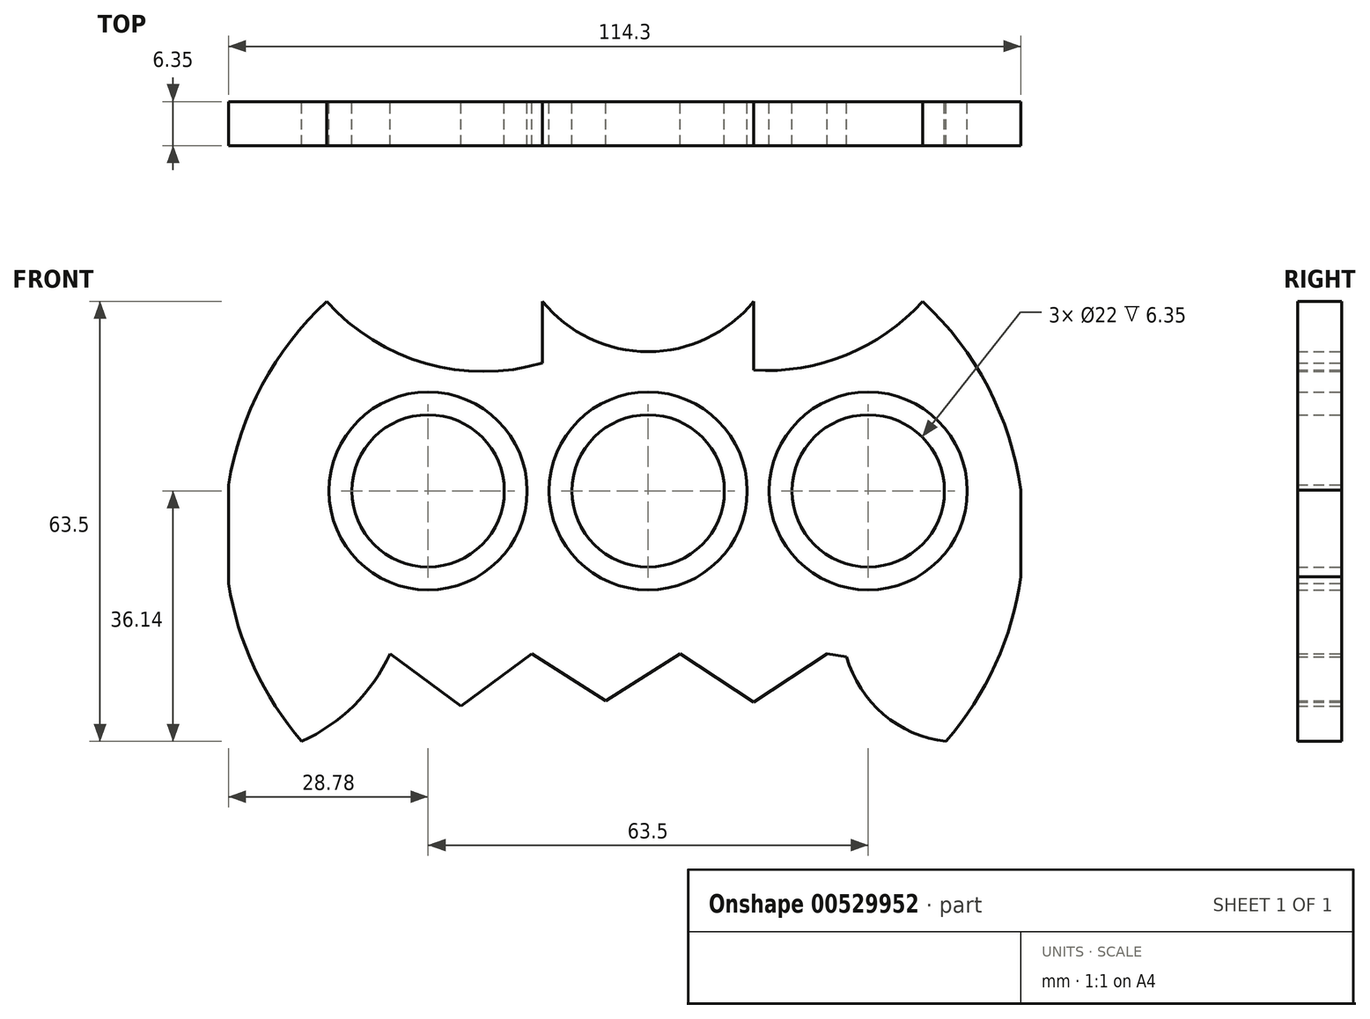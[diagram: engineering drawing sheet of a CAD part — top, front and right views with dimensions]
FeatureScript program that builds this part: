
annotation { "Feature Type Name" : "Feature", "Feature Type Description" : "" }
export const myFeature = defineFeature(function(context is Context, id is Id, definition is map)
    precondition{}
    {
        {
            var Q0;
            Q0=qCreatedBy(makeId("Front.planeOp"),FACE);
            var sketch = newSketch(context, id + "F0", { "sketchPlane" : qUnion([Q0])});
            skCircle(sketch, "E0", {"center": v(0, 0) * mm, "radius": 14.29 * mm});
            skCircle(sketch, "E1", {"center": v(0, 0) * mm, "radius": 11 * mm});
            skCircle(sketch, "E2", {"center": v(-31.75, 0) * mm, "radius": 14.29 * mm});
            skCircle(sketch, "E3", {"center": v(-31.75, 0) * mm, "radius": 11 * mm});
            skCircle(sketch, "E4", {"center": v(31.75, 0) * mm, "radius": 14.29 * mm});
            skCircle(sketch, "E5", {"center": v(31.75, 0) * mm, "radius": 11 * mm});
            skSolve(sketch);
        }
        {
            var Q0;
            Q0=qCreatedBy(makeId("Front.planeOp"),FACE);
            var sketch = newSketch(context, id + "F1", { "sketchPlane" : qUnion([Q0])});
            skArc(sketch, "E6.0", {"start": v(-46.36, 27.36) * mm, "mid": v(-61.02, -3.66) * mm, "end": v(-49.97, -36.14) * mm});
            skArc(sketch, "E7.0", {"start": v(-46.36, 27.36) * mm, "mid": v(-32.1, 18.4) * mm, "end": v(-15.24, 18.47) * mm});
            skPoint(sketch, "E8.0", {"position": v(-15.24, 22.92) * mm});
            skArc(sketch, "E9.0", {"start": v(-15.24, 27.36) * mm, "mid": v(0, 20.1) * mm, "end": v(15.24, 27.36) * mm});
            skPoint(sketch, "E10.0", {"position": v(28.55, 19.61) * mm});
            skArc(sketch, "E11.0", {"start": v(42.97, -36.14) * mm, "mid": v(54.13, -3.7) * mm, "end": v(39.6, 27.36) * mm});
            skLineSegment(sketch, "E12.0.0", {"start": v(25.82, -23.5) * mm, "end": v(28.64, -23.93) * mm});
            skArc(sketch, "E12.0.1", {"start": v(28.64, -23.93) * mm, "mid": v(33.92, -32.24) * mm, "end": v(42.97, -36.14) * mm});
            skArc(sketch, "E12.0.2", {"start": v(42.97, -36.14) * mm, "mid": v(50.1, -25.04) * mm, "end": v(53.77, -12.37) * mm});
            skLineSegment(sketch, "E12.0.3", {"start": v(53.77, -12.37) * mm, "end": v(53.77, 0.1) * mm});
            skArc(sketch, "E12.0.4", {"start": v(53.77, 0.1) * mm, "mid": v(49.04, 14.96) * mm, "end": v(39.6, 27.36) * mm});
            skArc(sketch, "E12.0.5", {"start": v(39.6, 27.36) * mm, "mid": v(28.55, 19.61) * mm, "end": v(15.24, 17.44) * mm});
            skLineSegment(sketch, "E12.0.6", {"start": v(15.24, 17.44) * mm, "end": v(15.24, 27.36) * mm});
            skArc(sketch, "E12.0.7", {"start": v(15.24, 27.36) * mm, "mid": v(0, 20.1) * mm, "end": v(-15.24, 27.36) * mm});
            skLineSegment(sketch, "E12.0.8", {"start": v(-15.24, 27.36) * mm, "end": v(-15.24, 18.47) * mm});
            skArc(sketch, "E12.0.9", {"start": v(-15.24, 18.47) * mm, "mid": v(-32.1, 18.4) * mm, "end": v(-46.36, 27.36) * mm});
            skArc(sketch, "E12.0.10", {"start": v(-46.36, 27.36) * mm, "mid": v(-55.69, 15.3) * mm, "end": v(-60.53, 0.86) * mm});
            skLineSegment(sketch, "E12.0.11", {"start": v(-60.53, 0.86) * mm, "end": v(-60.53, -13.36) * mm});
            skArc(sketch, "E12.0.12", {"start": v(-60.53, -13.36) * mm, "mid": v(-56.85, -25.49) * mm, "end": v(-49.97, -36.14) * mm});
            skArc(sketch, "E12.0.13", {"start": v(-49.97, -36.14) * mm, "mid": v(-42.45, -30.98) * mm, "end": v(-37.23, -23.5) * mm});
            skLineSegment(sketch, "E12.0.14", {"start": v(-37.23, -23.5) * mm, "end": v(-27.02, -31.06) * mm});
            skLineSegment(sketch, "E12.0.15", {"start": v(-27.02, -31.06) * mm, "end": v(-16.81, -23.5) * mm});
            skLineSegment(sketch, "E12.0.16", {"start": v(-16.81, -23.5) * mm, "end": v(-6.09, -30.3) * mm});
            skLineSegment(sketch, "E12.0.17", {"start": v(-6.09, -30.3) * mm, "end": v(4.63, -23.5) * mm});
            skLineSegment(sketch, "E12.0.18", {"start": v(4.63, -23.5) * mm, "end": v(15.23, -30.5) * mm});
            skLineSegment(sketch, "E12.0.19", {"start": v(15.23, -30.5) * mm, "end": v(25.82, -23.5) * mm});
            skSolve(sketch);
        }
        {
            var Q0;
            Q0=qCreatedBy(makeId("Front.planeOp"),FACE);
            var sketch = newSketch(context, id + "F2", { "sketchPlane" : qUnion([Q0])});
            skCircle(sketch, "E13.0", {"center": v(-31.75, 0) * mm, "radius": 14.29 * mm});
            skCircle(sketch, "E14.0", {"center": v(-31.75, 0) * mm, "radius": 11 * mm});
            skCircle(sketch, "E15.0", {"center": v(0, 0) * mm, "radius": 14.29 * mm});
            skCircle(sketch, "E16.0", {"center": v(0, 0) * mm, "radius": 11 * mm});
            skCircle(sketch, "E17.0", {"center": v(31.75, 0) * mm, "radius": 14.29 * mm});
            skCircle(sketch, "E18.0", {"center": v(31.75, 0) * mm, "radius": 11 * mm});
            skSolve(sketch);
        }
        {
            var Q0;
            Q0=qCreatedBy(makeId("Front.planeOp"),FACE);
            var sketch = newSketch(context, id + "F3", { "sketchPlane" : qUnion([Q0])});
            skArc(sketch, "E19.0", {"start": v(-46.36, 27.36) * mm, "mid": v(-61.02, -3.66) * mm, "end": v(-49.97, -36.14) * mm});
            skArc(sketch, "E20.0", {"start": v(-49.97, -36.14) * mm, "mid": v(-42.45, -30.98) * mm, "end": v(-37.23, -23.5) * mm});
            skPoint(sketch, "E21.0", {"position": v(-32.12, -27.28) * mm});
            skLineSegment(sketch, "E22.0", {"start": v(-37.23, -23.5) * mm, "end": v(-27.02, -31.06) * mm});
            skLineSegment(sketch, "E23.0", {"start": v(-27.02, -31.06) * mm, "end": v(-16.81, -23.5) * mm});
            skLineSegment(sketch, "E24.0", {"start": v(-16.81, -23.5) * mm, "end": v(-6.09, -30.3) * mm});
            skLineSegment(sketch, "E25.0", {"start": v(-6.09, -30.3) * mm, "end": v(4.63, -23.5) * mm});
            skLineSegment(sketch, "E26.0", {"start": v(4.63, -23.5) * mm, "end": v(15.23, -30.5) * mm});
            skLineSegment(sketch, "E27.0", {"start": v(15.23, -30.5) * mm, "end": v(25.82, -23.5) * mm});
            skPoint(sketch, "E28.0", {"position": v(27.23, -23.71) * mm});
            skArc(sketch, "E29.0", {"start": v(28.64, -23.93) * mm, "mid": v(33.92, -32.24) * mm, "end": v(42.97, -36.14) * mm});
            skArc(sketch, "E30.0", {"start": v(42.97, -36.14) * mm, "mid": v(50.1, -25.04) * mm, "end": v(53.77, -12.37) * mm});
            skArc(sketch, "E31.0", {"start": v(53.77, 0.1) * mm, "mid": v(49.04, 14.96) * mm, "end": v(39.6, 27.36) * mm});
            skArc(sketch, "E32.0", {"start": v(42.97, -36.14) * mm, "mid": v(54.13, -3.7) * mm, "end": v(39.6, 27.36) * mm});
            skArc(sketch, "E33.0", {"start": v(39.6, 27.36) * mm, "mid": v(28.55, 19.61) * mm, "end": v(15.24, 17.44) * mm});
            skLineSegment(sketch, "E34.0", {"start": v(15.24, 17.44) * mm, "end": v(15.24, 27.36) * mm});
            skArc(sketch, "E35.0", {"start": v(15.24, 27.36) * mm, "mid": v(0, 20.1) * mm, "end": v(-15.24, 27.36) * mm});
            skLineSegment(sketch, "E36.0", {"start": v(-15.24, 27.36) * mm, "end": v(-15.24, 18.47) * mm});
            skArc(sketch, "E37.0", {"start": v(-46.36, 27.36) * mm, "mid": v(-32.1, 18.4) * mm, "end": v(-15.24, 18.47) * mm});
            skCircle(sketch, "E38.0", {"center": v(-31.75, 0) * mm, "radius": 14.29 * mm});
            skCircle(sketch, "E39.0", {"center": v(0, 0) * mm, "radius": 14.29 * mm});
            skCircle(sketch, "E40.0", {"center": v(31.75, 0) * mm, "radius": 14.29 * mm});
            skSolve(sketch);
        }
        {
            var Q0;
            Q0=makeQuery(id+"F1.imprint","IMPRINT",FACE,{"disambiguationData":[TD([[makeQuery(id+"F1.imprint","IMPRINT",EDGE,{"derivedFrom":sQuery(id+"F1.wireOp",EDGE,"E12.0.0")}),1.0]])]});
            var Q1;
            Q1=makeQuery(id+"F0.imprint","IMPRINT",FACE,{"disambiguationData":[TD([[makeQuery(id+"F0.imprint","IMPRINT",EDGE,{"derivedFrom":sQuery(id+"F0.wireOp",EDGE,"E2")}),1.0]])]});
            var Q2;
            Q2=makeQuery(id+"F0.imprint","IMPRINT",FACE,{"disambiguationData":[TD([[makeQuery(id+"F0.imprint","IMPRINT",EDGE,{"derivedFrom":sQuery(id+"F0.wireOp",EDGE,"E0")}),1.0]])]});
            var Q3;
            Q3=makeQuery(id+"F0.imprint","IMPRINT",FACE,{"disambiguationData":[TD([[makeQuery(id+"F0.imprint","IMPRINT",EDGE,{"derivedFrom":sQuery(id+"F0.wireOp",EDGE,"E4")}),1.0]])]});
            extrude(context, id + "F4", {"entities" : qUnion([Q0, Q1, Q2, Q3]), "depth" : 6.35 * mm, "offsetDistance" : 25.4 * mm});
        }
    });
